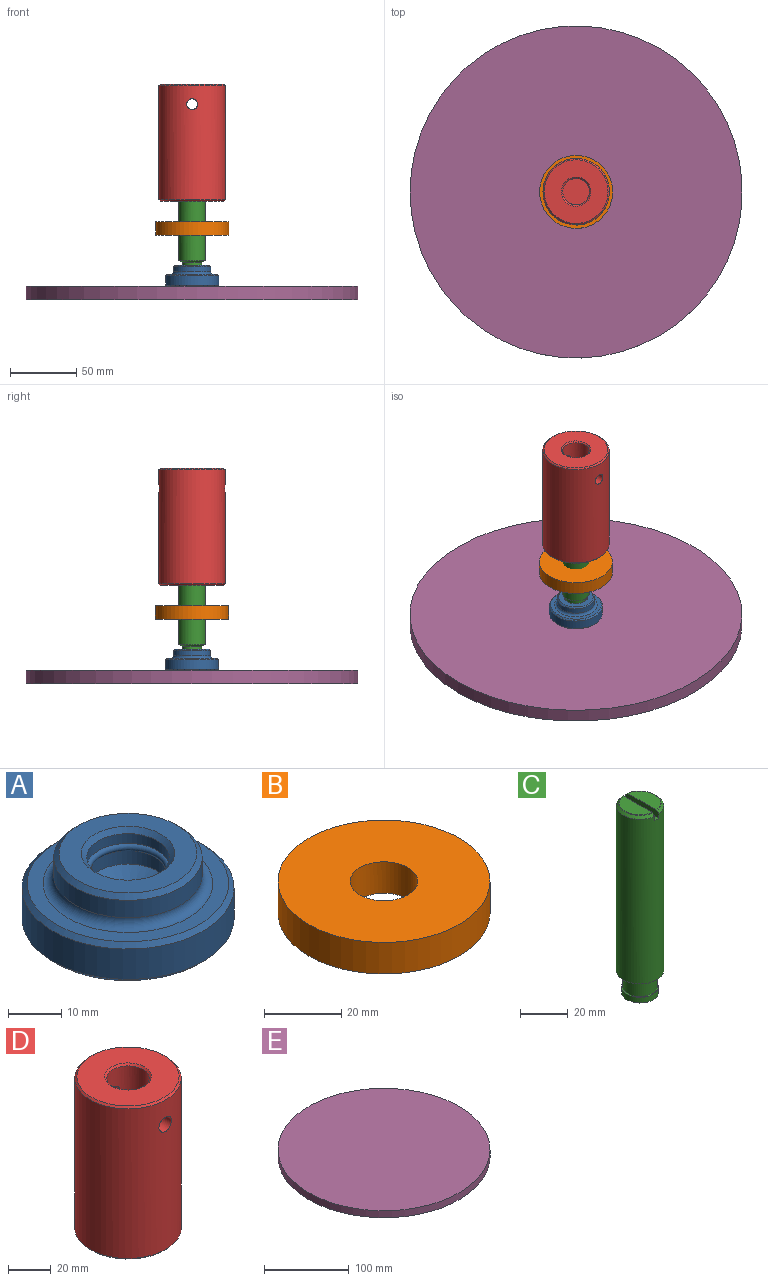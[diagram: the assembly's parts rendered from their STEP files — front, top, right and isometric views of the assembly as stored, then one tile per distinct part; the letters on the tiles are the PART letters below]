
ASSEMBLY  parts=5 mates=4
PART A: 16 faces, bbox 40x40x16 mm
  f0: torus R=7.8mm, axis (0,0,-1), area 108.4mm2, adj f8,f9
  f1: cone r=19.5mm half-angle=45deg, axis (0,0,1), area 173.3mm2, adj f2,f15
  f2: cylinder r=20mm len=40mm, axis (0,0,-1), area 879.6mm2, adj f1,f3
  f3: cone r=19.5mm half-angle=45deg, axis (0,0,-1), area 173.3mm2, adj f2,f14
  f4: torus R=16mm, axis (0,0,-1), area 290.7mm2, adj f5,f14
  f5: cylinder r=14mm len=28mm, axis (0,0,-1), area 351.9mm2, adj f4,f6
  f6: cone r=13.5mm half-angle=45deg, axis (0,0,-1), area 120mm2, adj f5,f13
  f7: cone r=8.3mm half-angle=45deg, axis (0,0,1), area 73.8mm2, adj f8,f13
  f8: cylinder r=7.8mm len=15.6mm, axis (0,0,-1), area 110.3mm2, adj f0,f7
  f9: cylinder r=7.8mm len=15.6mm, axis (0,0,-1), area 159.3mm2, adj f0,f10
  f10: cone r=3.9mm half-angle=60deg, axis (0,0,1), area 220.7mm2, adj f9
  f11: cylinder r=7.8mm len=15.6mm, axis (0,0,-1), area 49mm2, adj f12,f15
  f12: plane 15.6x15.6mm, normal (0,0,-1), area 191.1mm2, adj f11
  f13: plane 26x26mm, normal (0,0,1), area 287.6mm2, adj f6,f7
  f14: plane 38x38mm, normal (0,0,1), area 329.9mm2, adj f3,f4
  f15: plane 38x38mm, normal (0,0,-1), area 943mm2, adj f1,f11
PART B: 4 faces, bbox 55x55x10 mm
  f0: cylinder r=27.5mm len=55mm, axis (0,0,1), area 1727.9mm2, adj f1,f2
  f1: plane 55x55mm, normal (0,0,-1), area 2135.3mm2, adj f0,f3
  f2: plane 55x55mm, normal (0,0,1), area 2135.3mm2, adj f0,f3
  f3: cylinder r=8.75mm len=17.5mm, axis (0,0,1), area 549.8mm2, adj f1,f2
PART C: 15 faces, bbox 20x20x100 mm
  f0: sphere r=13mm, area 209.3mm2, adj f1
  f1: cylinder r=7.75mm len=15.5mm, axis (0,0,-1), area 143mm2, adj f0,f14
  f2: cylinder r=7.2mm len=14.4mm, axis (0,0,-1), area 323.5mm2, adj f3,f14
  f3: cone r=8.6mm half-angle=64.3deg, axis (0,0,1), area 168mm2, adj f2,f4
  f4: cylinder r=10mm len=84.65mm, axis (0,0,-1), area 5307.9mm2, adj f3,f7,f8,f9,f10,f11
  f5: cone r=9.32mm half-angle=60deg, axis (0,0,-1), area 6.4mm2, adj f9,f10,f12
  f6: cone r=9.32mm half-angle=60deg, axis (0,0,-1), area 6.4mm2, adj f7,f8,f13
  f7: cone r=9.38mm half-angle=42.8deg, axis (0,0,-1), area 45.2mm2, adj f4,f6,f8
  f8: plane 19.84x3.5mm, normal (-1,0,0), area 67.7mm2, adj f4,f6,f7,f11,f13
  f9: cone r=9.38mm half-angle=42.8deg, axis (0,0,-1), area 45.2mm2, adj f4,f5,f10
  f10: plane 19.84x3.5mm, normal (1,0,0), area 67.7mm2, adj f4,f5,f9,f11,f12
  f11: plane 20x2.5mm, normal (0,0,1), area 49.9mm2, adj f4,f8,f10
  f12: plane 17.11x7.4mm, normal (0,0,1), area 95.9mm2, adj f5,f10
  f13: plane 17.11x7.4mm, normal (0,0,1), area 95.9mm2, adj f6,f8
  f14: plane 15.5x15.5mm, normal (0,0,1), area 25.8mm2, adj f1,f2
PART D: 12 faces, bbox 50x50x88 mm
  f0: cylinder r=25mm len=86mm, axis (0,0,-1), area 13402.6mm2, adj f4,f6,f7,f9
  f1: cylinder r=10mm len=27mm, axis (0,0,-1), area 1588.6mm2, adj f3,f5,f6,f7
  f2: plane 48x48mm, normal (0,0,1), area 1429.4mm2, adj f4,f5
  f3: plane 20x20mm, normal (0,0,1), area 314.2mm2, adj f1
  f4: cone r=25mm half-angle=45deg, axis (0,0,-1), area 217.7mm2, adj f0,f2
  f5: cone r=11mm half-angle=45deg, axis (0,0,1), area 93.3mm2, adj f1,f2
  f6: cylinder r=4.1mm len=15.88mm, axis (0,1,0), area 393.3mm2, adj f0,f1
  f7: cylinder r=4.1mm len=15.88mm, axis (0,-1,0), area 393.3mm2, adj f0,f1
  f8: plane 48x48mm, normal (0,0,-1), area 1569mm2, adj f9,f11
  f9: cone r=24mm half-angle=45deg, axis (0,0,1), area 217.7mm2, adj f0,f8
  f10: cone r=0mm half-angle=59deg, axis (0,0,-1), area 280.6mm2, adj f11
  f11: cylinder r=8.75mm len=50mm, axis (0,0,-1), area 2748.9mm2, adj f8,f10
PART E: 3 faces, bbox 250x250x10 mm
  f0: cylinder r=125mm len=250mm, axis (0,0,1), area 7854mm2, adj f1,f2
  f1: plane 250x250mm, normal (0,0,-1), area 49087.4mm2, adj f0
  f2: plane 250x250mm, normal (0,0,1), area 49087.4mm2, adj f0
PLACE A rot(axis=(0,0,1),180deg) t=(-14.02,-12.73,-72.02)mm
PLACE B t=(-14.02,-12.73,59)mm
PLACE C t=(-14.02,-12.73,-72.18)mm
PLACE D t=(-14.02,-12.73,74.47)mm
PLACE E t=(-14.02,-12.73,20.38)mm
MATE fastened A.f0 <-> C.f1  axis (0,0,-1) through (-14.02,-12.73,-69.62)mm
MATE fastened E.f0 <-> A.f11  axis (0,0,1) through (-14.02,-12.73,-77.62)mm
MATE slider B.f3 <-> C.f1  axis (0,0,1) through (-14.02,-12.73,-29)mm
MATE fastened C.f1 <-> D.f4  axis (0,0,-1) through (-14.02,-12.73,26.47)mm
